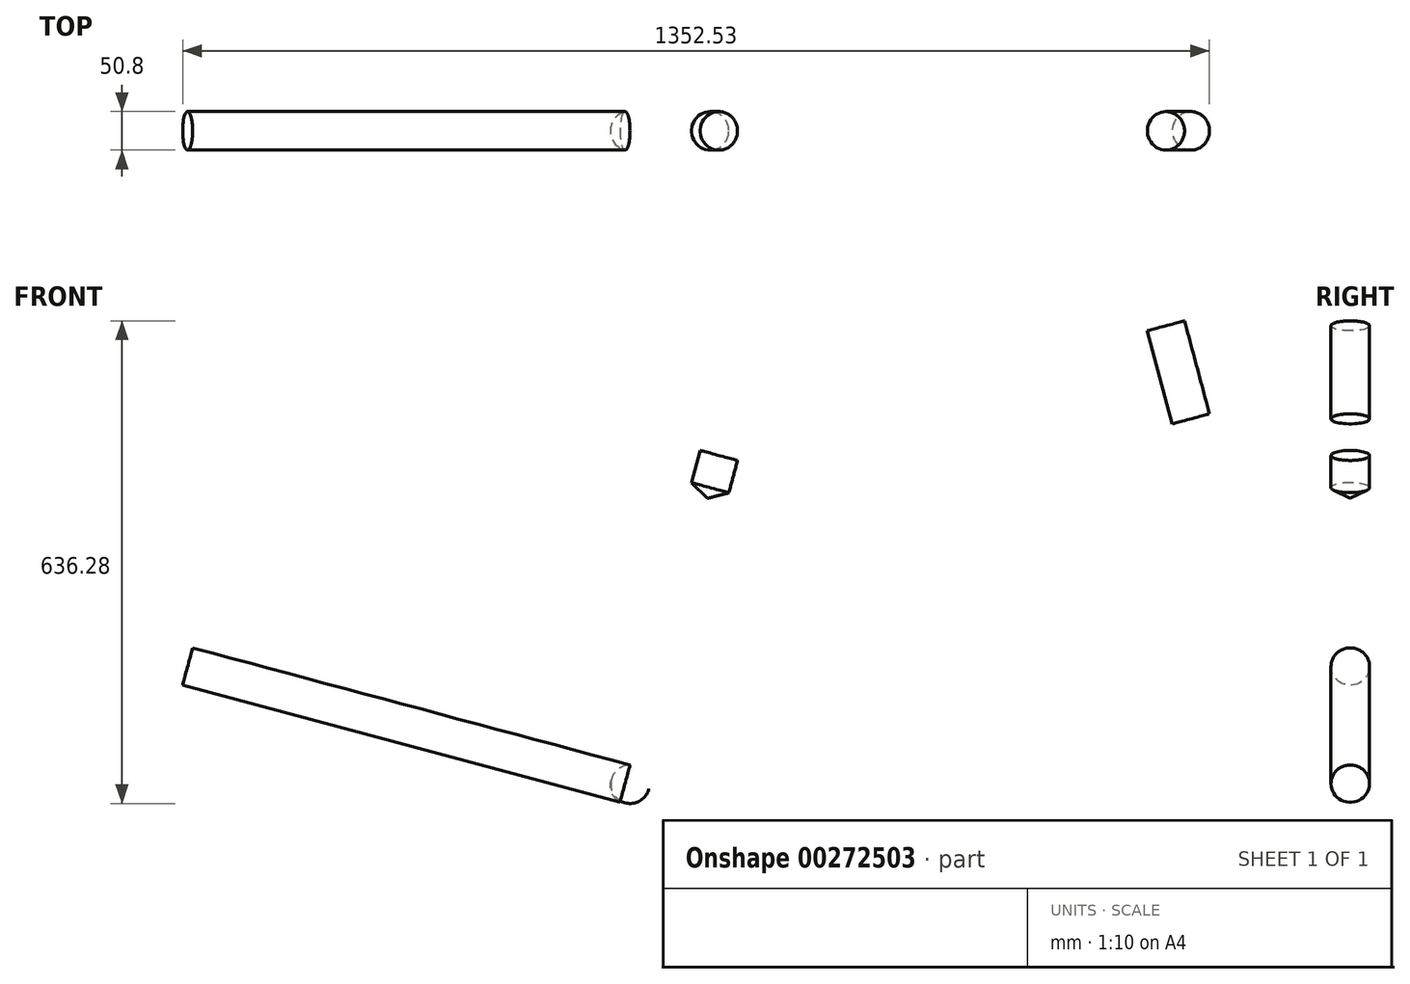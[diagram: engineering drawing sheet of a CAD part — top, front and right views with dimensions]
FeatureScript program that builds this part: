
annotation { "Feature Type Name" : "Feature", "Feature Type Description" : "" }
export const myFeature = defineFeature(function(context is Context, id is Id, definition is map)
    precondition{}
    {
        {
            var Q0;
            Q0=qCreatedBy(makeId("Front.planeOp"),FACE);
            var sketch = newSketch(context, id + "F0", { "sketchPlane" : qUnion([Q0])});
            skCircle(sketch, "E0", {"center": v(0, 0) * mm, "radius": 25.4 * mm});
            skLineSegment(sketch, "E1", {"start": v(-575.68, 181.45) * mm, "end": v(13.15, 23.67) * mm});
            skLineSegment(sketch, "E2", {"start": v(-588.83, 132.38) * mm, "end": v(0, -25.4) * mm});
            skLineSegment(sketch, "E3", {"start": v(-588.83, 132.38) * mm, "end": v(-575.68, 181.45) * mm});
            skPoint(sketch, "E4", {"position": v(0, 25.4) * mm});
            skPoint(sketch, "E5", {"position": v(0, -25.4) * mm});
            skLineSegment(sketch, "E6", {"start": v(92.93, 441.62) * mm, "end": v(-25.4, 0) * mm});
            skLineSegment(sketch, "E7", {"start": v(142, 428.47) * mm, "end": v(23.67, -13.15) * mm});
            skLineSegment(sketch, "E8", {"start": v(92.93, 441.62) * mm, "end": v(142, 428.47) * mm});
            skPoint(sketch, "E9", {"position": v(-25.4, 0) * mm});
            skPoint(sketch, "E10", {"position": v(25.4, 0) * mm});
            skLineSegment(sketch, "E11.0", {"start": v(-25.4, 0) * mm, "end": v(23.67, -13.15) * mm, "construction": true});
            skLineSegment(sketch, "E12", {"start": v(142, 428.47) * mm, "end": v(688.33, 574.86) * mm});
            skLineSegment(sketch, "E13", {"start": v(688.33, 574.86) * mm, "end": v(708.06, 501.26) * mm});
            skLineSegment(sketch, "E14", {"start": v(708.06, 501.26) * mm, "end": v(119.23, 343.48) * mm});
            skLineSegment(sketch, "E15", {"start": v(-659.96, 177.73) * mm, "end": v(312.84, -82.93) * mm});
            skPoint(sketch, "E16", {"position": v(-582.25, 156.91) * mm});
            skLineSegment(sketch, "E17", {"start": v(0, -25.4) * mm, "end": v(13.15, 23.67) * mm});
            skLineSegment(sketch, "E18", {"start": v(-25.4, 0) * mm, "end": v(23.67, -13.15) * mm});
            skLineSegment(sketch, "E19", {"start": v(141.37, 524.24) * mm, "end": v(-51.62, -196) * mm});
            skPoint(sketch, "E20.positionSnap0", {"position": v(117.47, 435.05) * mm});
            skLineSegment(sketch, "E21", {"start": v(688.33, 574.86) * mm, "end": v(681.76, 599.4) * mm});
            skLineSegment(sketch, "E22", {"start": v(681.76, 599.4) * mm, "end": v(730.83, 612.55) * mm});
            skLineSegment(sketch, "E23", {"start": v(708.06, 501.26) * mm, "end": v(714.63, 476.72) * mm});
            skLineSegment(sketch, "E24", {"start": v(714.63, 476.72) * mm, "end": v(763.7, 489.87) * mm});
            skLineSegment(sketch, "E25", {"start": v(763.7, 489.87) * mm, "end": v(730.83, 612.55) * mm});
            skLineSegment(sketch, "E26", {"start": v(668.8, 745.88) * mm, "end": v(790.97, 289.94) * mm});
            skPoint(sketch, "E27", {"position": v(706.3, 605.97) * mm});
            skLineSegment(sketch, "E28", {"start": v(-189.15, 300.3) * mm, "end": v(809.67, 567.93) * mm});
            skPoint(sketch, "E29", {"position": v(698.2, 538.06) * mm});
            skSolve(sketch);
        }
        {
            var Q0;
            {var subQ0=sQuery(id+"F0.wireOp",EDGE,"E3");var subQ1=sQuery(id+"F0.wireOp",EDGE,"E2");var subQ2=makeQuery(id+"F0.imprint","INTERSECT",VERTEX,{"derivedFrom":[subQ1,subQ0]});Q0=makeQuery(id+"F0.imprint","IMPRINT",FACE,{"disambiguationData":[TD([[makeQuery(id+"F0.imprint","IMPRINT",EDGE,{"disambiguationData":[TD([[subQ2,-1.0]])],"derivedFrom":subQ1}),1.0]])]});}
            var Q1;
            Q1=sQuery(id+"F0.wireOp",EDGE,"E15");
            revolve(context, id + "F1", {"surfaceOperationType" : NewSurfaceOperationType.NEW, "entities" : qUnion([Q0]), "axis" : qUnion([Q1]), "revolveType" : RevolveType.FULL});
        }
        {
            var Q0;
            {var subQ3=sQuery(id+"F0.wireOp",EDGE,"E28");var subQ5=sQuery(id+"F0.wireOp",EDGE,"E19");var subQ7=makeQuery(id+"F0.imprint","INTERSECT",VERTEX,{"derivedFrom":[subQ5,subQ3]});Q0=makeQuery(id+"F0.imprint","IMPRINT",FACE,{"disambiguationData":[TD([[makeQuery(id+"F0.imprint","IMPRINT",EDGE,{"disambiguationData":[TD([[subQ7,1.0]])],"derivedFrom":subQ5}),1.0]])]});}
            var Q1;
            {var subQ9=sQuery(id+"F0.wireOp",EDGE,"E0");var subQ10=makeQuery(id+"F0.imprint","IMPRINT",VERTEX,{"derivedFrom":subQ9});Q1=makeQuery(id+"F0.imprint","IMPRINT",FACE,{"disambiguationData":[TD([[makeQuery(id+"F0.imprint","IMPRINT",EDGE,{"disambiguationData":[TD([[subQ10,1.0]])],"derivedFrom":subQ9}),-1.0]])]});}
            var Q2;
            Q2=sQuery(id+"F0.wireOp",EDGE,"E19");
            revolve(context, id + "F2", {"operationType" : NewBodyOperationType.ADD, "surfaceOperationType" : NewSurfaceOperationType.NEW, "entities" : qUnion([Q0, Q1]), "axis" : qUnion([Q2]), "revolveType" : RevolveType.FULL});
        }
        {
            var Q0;
            {var subQ1=sQuery(id+"F0.wireOp",EDGE,"E23");Q0=makeQuery(id+"F0.imprint","IMPRINT",FACE,{"disambiguationData":[TD([[makeQuery(id+"F0.imprint","IMPRINT",EDGE,{"derivedFrom":subQ1}),1.0]])]});}
            var Q1;
            {var subQ5=sQuery(id+"F0.wireOp",EDGE,"E21");Q1=makeQuery(id+"F0.imprint","IMPRINT",FACE,{"disambiguationData":[TD([[makeQuery(id+"F0.imprint","IMPRINT",EDGE,{"derivedFrom":subQ5}),-1.0]])]});}
            var Q2;
            Q2=sQuery(id+"F0.wireOp",EDGE,"E26");
            revolve(context, id + "F3", {"operationType" : NewBodyOperationType.ADD, "surfaceOperationType" : NewSurfaceOperationType.NEW, "entities" : qUnion([Q0, Q1]), "axis" : qUnion([Q2]), "revolveType" : RevolveType.FULL});
        }
    });
